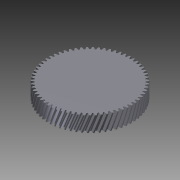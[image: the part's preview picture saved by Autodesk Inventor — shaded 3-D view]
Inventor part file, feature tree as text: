
AUTODESK INVENTOR PART (.ipt)
format: ipt  version: 2012 (Build 160160000, 160)  size: 970,240 bytes
history: native  units: mm (DEFAULTED — no unit token found)
features: plane x3, other x3, sketch x3, extrude x2, reference x1
ambient origin geometry x8: Origin, YZ Plane, XZ Plane, XY Plane, X Axis, Y Axis, Z Axis, Center Point
bodies: Solid1 (feature_tree)
feature tree (12):
  extrude  "Extrusion1"  Depth=4.0mm TaperAngle=0.0deg
  plane  "Work Plane2"
  plane  "Work Plane8"
  plane  "Work Plane9"
  other  "Spur Gear"
  extrude  "Extrusion2"  Depth=10.0mm TaperAngle=0.0deg
  sketch  "Sketch1"  dims[d0=21.912015mm d1=4.0mm d2=0.0mm]
  sketch  "Sketch2"  dims[d3=21.280799mm d4=10.0mm d5=0.0mm]
  other  "Srf1"
  sketch  "Sketch3"  dims[d16=18.071789mm d17=0.0mm d34=0.498666mm d39=0.0mm d41=0.0mm d43=18.071789mm d46=18.071789mm d47=0.0mm d48=0.0mm d49=2.0mm d50=0.0mm]
  reference  "Reference1"
  other  "Pitch Diameter"
